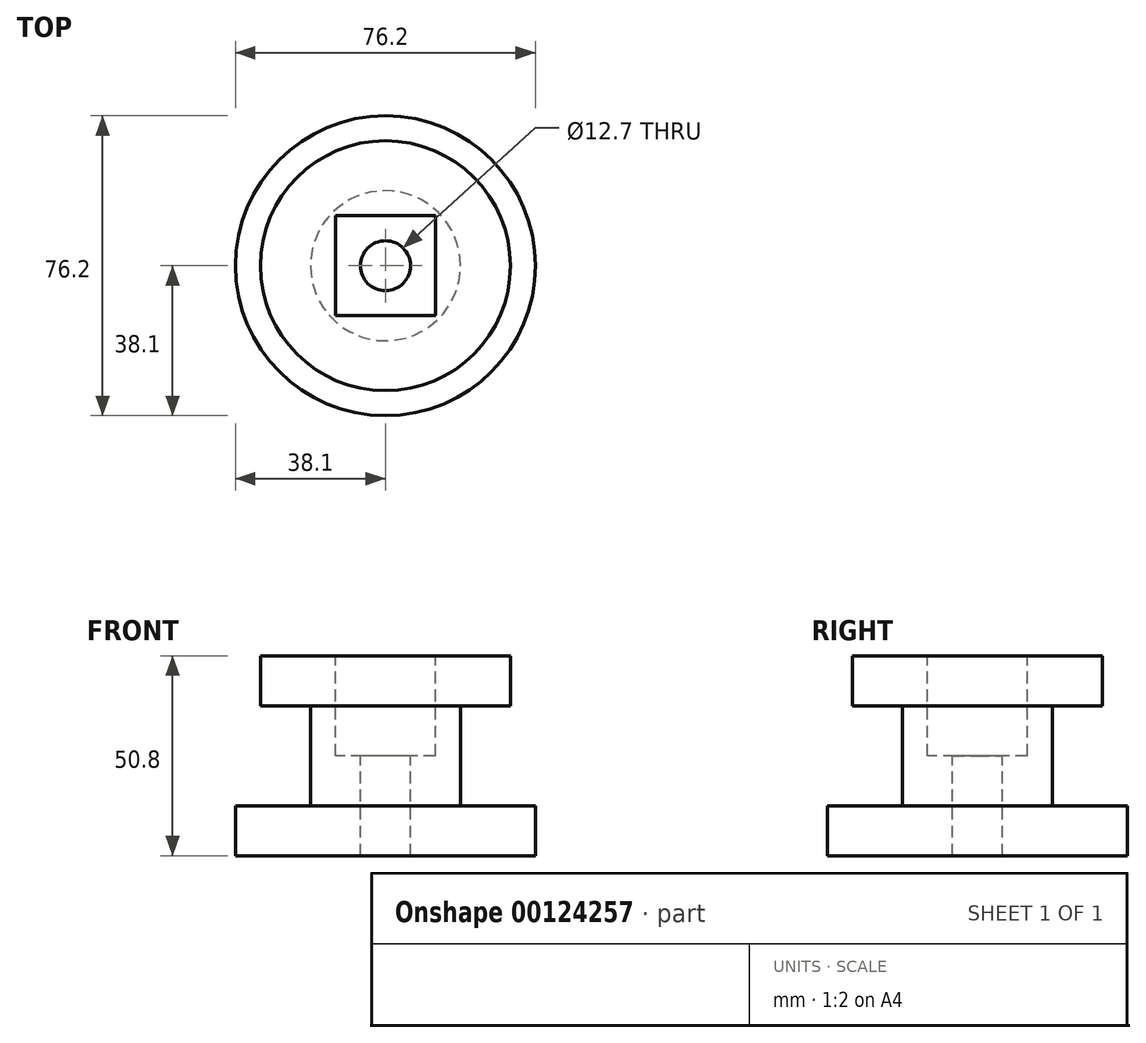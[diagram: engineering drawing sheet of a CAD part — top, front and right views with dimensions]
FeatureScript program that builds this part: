
annotation { "Feature Type Name" : "Feature", "Feature Type Description" : "" }
export const myFeature = defineFeature(function(context is Context, id is Id, definition is map)
    precondition{}
    {
        {
            var Q0;
            Q0=qCreatedBy(makeId("Top.planeOp"),FACE);
            var sketch = newSketch(context, id + "F0", { "sketchPlane" : qUnion([Q0])});
            skCircle(sketch, "E0", {"center": v(0, 0) * mm, "radius": 38.1 * mm});
            skSolve(sketch);
        }
        {
            var Q0;
            Q0 = qSketchRegion(id + "F0", true);
            extrude(context, id + "F1", {"entities" : qUnion([Q0]), "depth" : 12.7 * mm});
        }
        {
            var Q0;
            Q0=makeQuery(id+"F1.opExtrude","CAP_FACE",FACE,{"disambiguationData":[OSD([sQuery(id+"F0.wireOp",EDGE,"E0")])],"isStart":false});
            var sketch = newSketch(context, id + "F2", { "sketchPlane" : qUnion([Q0])});
            skCircle(sketch, "E1", {"center": v(0, 0) * mm, "radius": 19.05 * mm});
            skSolve(sketch);
        }
        {
            var Q0;
            Q0 = qSketchRegion(id + "F2", true);
            extrude(context, id + "F3", {"entities" : qUnion([Q0]), "operationType" : NewBodyOperationType.ADD, "depth" : 25.4 * mm});
        }
        {
            var Q0;
            Q0=makeQuery(id+"F3.opExtrude","CAP_FACE",FACE,{"disambiguationData":[OSD([sQuery(id+"F2.wireOp",EDGE,"E1")])],"isStart":false});
            var sketch = newSketch(context, id + "F4", { "sketchPlane" : qUnion([Q0])});
            skCircle(sketch, "E2", {"center": v(0, 0) * mm, "radius": 31.75 * mm});
            skSolve(sketch);
        }
        {
            var Q0;
            Q0 = qSketchRegion(id + "F4", true);
            extrude(context, id + "F5", {"entities" : qUnion([Q0]), "operationType" : NewBodyOperationType.ADD, "depth" : 12.7 * mm});
        }
        {
            var Q0;
            Q0=makeQuery(id+"F5.opExtrude","CAP_FACE",FACE,{"disambiguationData":[OSD([sQuery(id+"F4.wireOp",EDGE,"E2")])],"isStart":false});
            var sketch = newSketch(context, id + "F6", { "sketchPlane" : qUnion([Q0])});
            skLineSegment(sketch, "E3.bottom", {"start": v(12.7, 12.7) * mm, "end": v(-12.7, 12.7) * mm});
            skLineSegment(sketch, "E3.top", {"start": v(12.7, -12.7) * mm, "end": v(-12.7, -12.7) * mm});
            skLineSegment(sketch, "E3.left", {"start": v(12.7, 12.7) * mm, "end": v(12.7, -12.7) * mm});
            skLineSegment(sketch, "E3.right", {"start": v(-12.7, 12.7) * mm, "end": v(-12.7, -12.7) * mm});
            skPoint(sketch, "E3.middle", {"position": v(0, 0) * mm});
            skSolve(sketch);
        }
        {
            var Q0;
            Q0 = qSketchRegion(id + "F6", true);
            extrude(context, id + "F7", {"entities" : qUnion([Q0]), "operationType" : NewBodyOperationType.REMOVE, "oppositeDirection" : true, "depth" : 25.4 * mm});
        }
        {
            var Q0;
            Q0=makeQuery(id+"F5.opExtrude","CAP_FACE",FACE,{"disambiguationData":[OSD([sQuery(id+"F4.wireOp",EDGE,"E2")])],"isStart":false});
            var sketch = newSketch(context, id + "F8", { "sketchPlane" : qUnion([Q0])});
            skCircle(sketch, "E4", {"center": v(0, 0) * mm, "radius": 6.35 * mm});
            skSolve(sketch);
        }
        {
            var Q0;
            Q0 = qSketchRegion(id + "F8", true);
            extrude(context, id + "F9", {"entities" : qUnion([Q0]), "operationType" : NewBodyOperationType.REMOVE, "endBound" : BoundingType.THROUGH_ALL, "oppositeDirection" : true, "depth" : 25.4 * mm});
        }
    });
